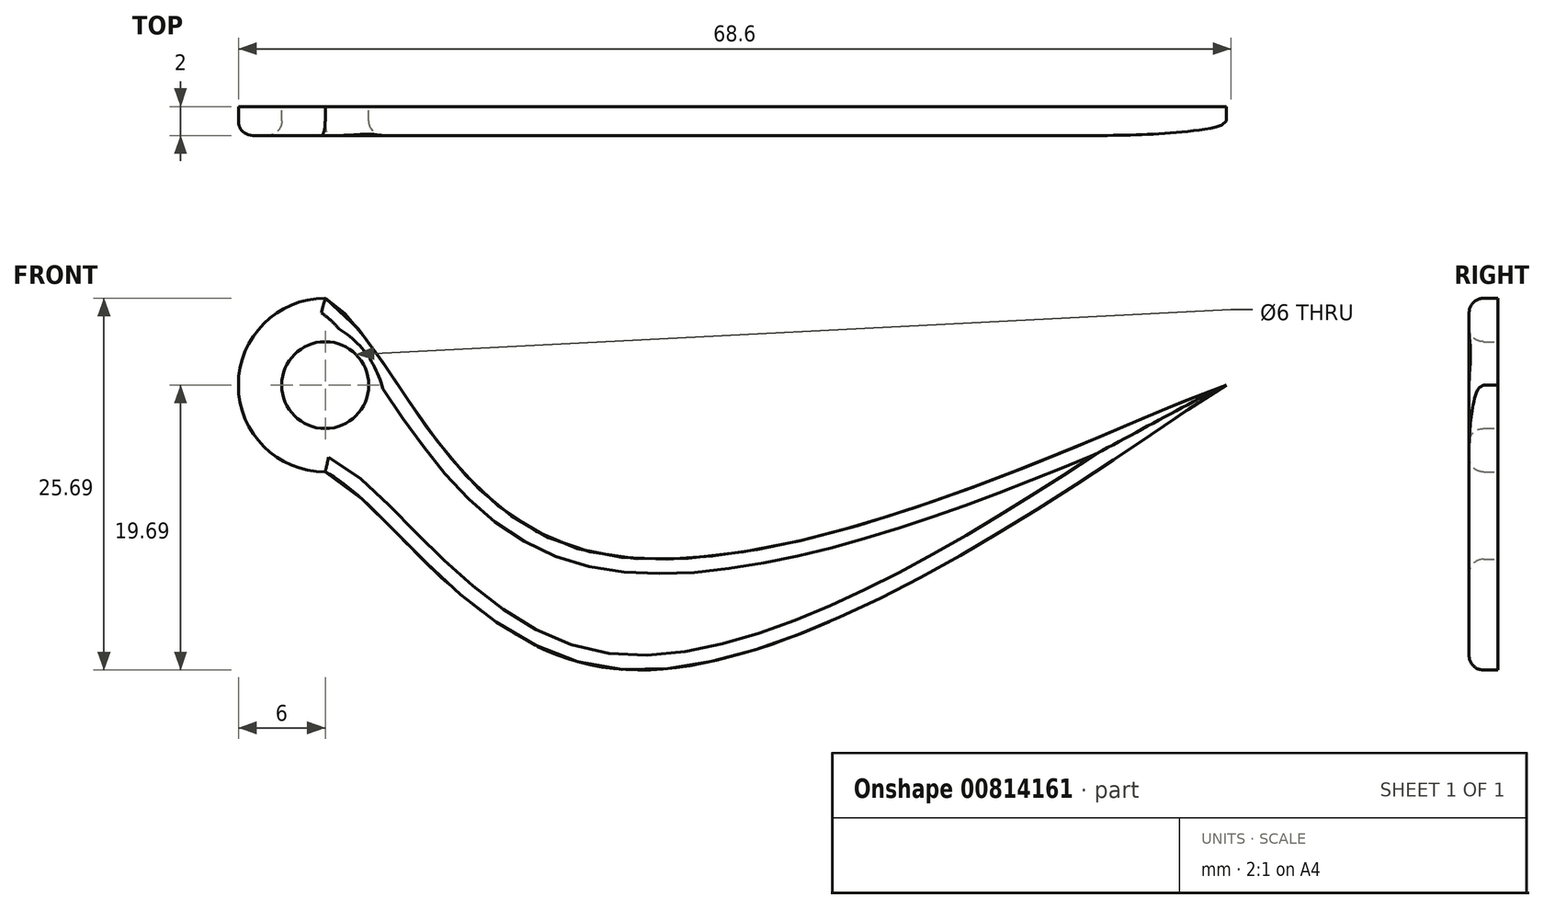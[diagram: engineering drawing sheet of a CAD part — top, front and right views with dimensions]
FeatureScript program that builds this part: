
annotation { "Feature Type Name" : "Feature", "Feature Type Description" : "" }
export const myFeature = defineFeature(function(context is Context, id is Id, definition is map)
    precondition{}
    {
        {
            var Q0;
            Q0=qCreatedBy(makeId("Front.planeOp"),FACE);
            var sketch = newSketch(context, id + "F0", { "sketchPlane" : qUnion([Q0])});
            skCircle(sketch, "E0", {"center": v(0, 0) * mm, "radius": 3 * mm});
            skArc(sketch, "E1", {"start": v(0, 6) * mm, "mid": v(-6, 0) * mm, "end": v(0, -6) * mm});
            skFitSpline(sketch, "E2", {"points": [v(0, 6) * mm, v(17.32, -11.27) * mm, v(62.28, 0) * mm], "startDerivative": vector(31.28, -17.88) * mm, "endDerivative": vector(35.86, 11.9) * mm});
            skFitSpline(sketch, "E3", {"points": [v(0, -6) * mm, v(20.3, -19.63) * mm, v(62.28, 0) * mm], "startDerivative": vector(32.76, -16.56) * mm, "endDerivative": vector(32.15, 19.06) * mm});
            skSolve(sketch);
        }
        {
            var Q0;
            Q0 = qSketchRegion(id + "F0", true);
            extrude(context, id + "F1", {"entities" : qUnion([Q0]), "depth" : 2 * mm, "offsetDistance" : 25 * mm});
        }
        {
            var Q0;
            Q0=makeQuery(id+"F1.opExtrude","CAP_EDGE",EDGE,{"disambiguationData":[OSD([sQuery(id+"F0.wireOp",EDGE,"E2")])],"isStart":false});
            var Q1;
            Q1=makeQuery(id+"F1.opExtrude","CAP_FACE",FACE,{"disambiguationData":[OSD([sQuery(id+"F0.wireOp",EDGE,"E0"),sQuery(id+"F0.wireOp",EDGE,"E1"),sQuery(id+"F0.wireOp",EDGE,"E2"),sQuery(id+"F0.wireOp",EDGE,"E3")])],"isStart":false});
            fillet(context, id + "F2", {"entities" : qUnion([Q0, Q1]), "radius" : 1 * mm, "tangentPropagation" : true, "allowEdgeOverflow" : false});
        }
    });
